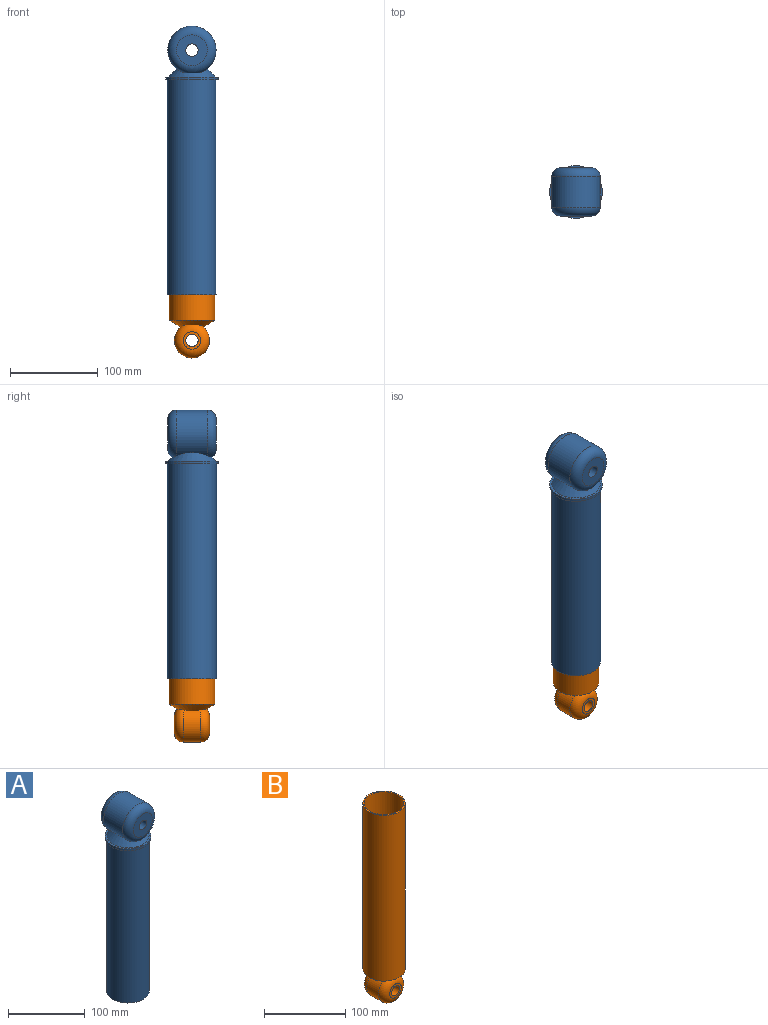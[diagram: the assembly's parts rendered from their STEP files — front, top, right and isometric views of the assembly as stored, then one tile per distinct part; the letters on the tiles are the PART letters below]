
ASSEMBLY  parts=2 mates=1
PART A: 14 faces, bbox 60x60x308.8 mm
  f0: cylinder r=27.5mm len=55mm, axis (0,1,0), area 4858.8mm2, adj f3,f4,f6
  f1: plane 35x35mm, normal (0,-1,0), area 808.2mm2, adj f4,f5
  f2: plane 35x35mm, normal (0,1,0), area 808.2mm2, adj f3,f5
  f3: torus R=17.5mm, axis (0,-1,0), area 2263.3mm2, adj f0,f2,f6
  f4: torus R=17.5mm, axis (0,-1,0), area 2263.3mm2, adj f0,f1,f6
  f5: cylinder r=7mm len=55mm, axis (0,-1,0), area 2419mm2, adj f1,f2
  f6: cone r=27.5mm half-angle=45deg, axis (0,0,-1), area 1540.8mm2, adj f0,f3,f4,f9
  f7: cylinder r=30mm len=60mm, axis (0,0,1), area 565.5mm2, adj f8,f9
  f8: plane 60x60mm, normal (0,0,-1), area 364.4mm2, adj f7,f11
  f9: plane 60x60mm, normal (0,0,1), area 451.6mm2, adj f6,f7
  f10: cylinder r=26mm len=245mm, axis (0,0,1), area 40023.9mm2, adj f12,f13
  f11: cylinder r=28mm len=245mm, axis (0,0,1), area 43102.7mm2, adj f8,f12
  f12: plane 56x56mm, normal (0,0,-1), area 339.3mm2, adj f10,f11
  f13: plane 52x52mm, normal (0,0,-1), area 2123.7mm2, adj f10
PART B: 11 faces, bbox 52x52x294.6 mm
  f0: cylinder r=20mm len=40mm, axis (0,1,0), area 1978.5mm2, adj f3,f4,f6
  f1: plane 20x20mm, normal (0,-1,0), area 160.2mm2, adj f4,f5
  f2: plane 20x20mm, normal (0,1,0), area 160.2mm2, adj f3,f5
  f3: torus R=10mm, axis (0,-1,0), area 1491.4mm2, adj f0,f2,f6
  f4: torus R=10mm, axis (0,-1,0), area 1491.4mm2, adj f0,f1,f6
  f5: cylinder r=7mm len=40mm, axis (0,-1,0), area 1759.3mm2, adj f1,f2
  f6: cone r=26mm half-angle=59.3deg, axis (0,0,1), area 1633.2mm2, adj f0,f3,f4,f8
  f7: cylinder r=24.5mm len=250mm, axis (0,0,-1), area 38484.5mm2, adj f9,f10
  f8: cylinder r=26mm len=250mm, axis (0,0,-1), area 40840.7mm2, adj f6,f9
  f9: plane 52x52mm, normal (0,0,1), area 238mm2, adj f7,f8
  f10: plane 49x49mm, normal (0,0,1), area 1885.7mm2, adj f7
PLACE A t=(-153.37,-143.55,45.75)mm fixed
PLACE B t=(-153.37,-143.55,-285.25)mm
MATE slider B.f7 <-> A.f10  axis (0,0,1) through (-153.37,-143.55,-12.25)mm
